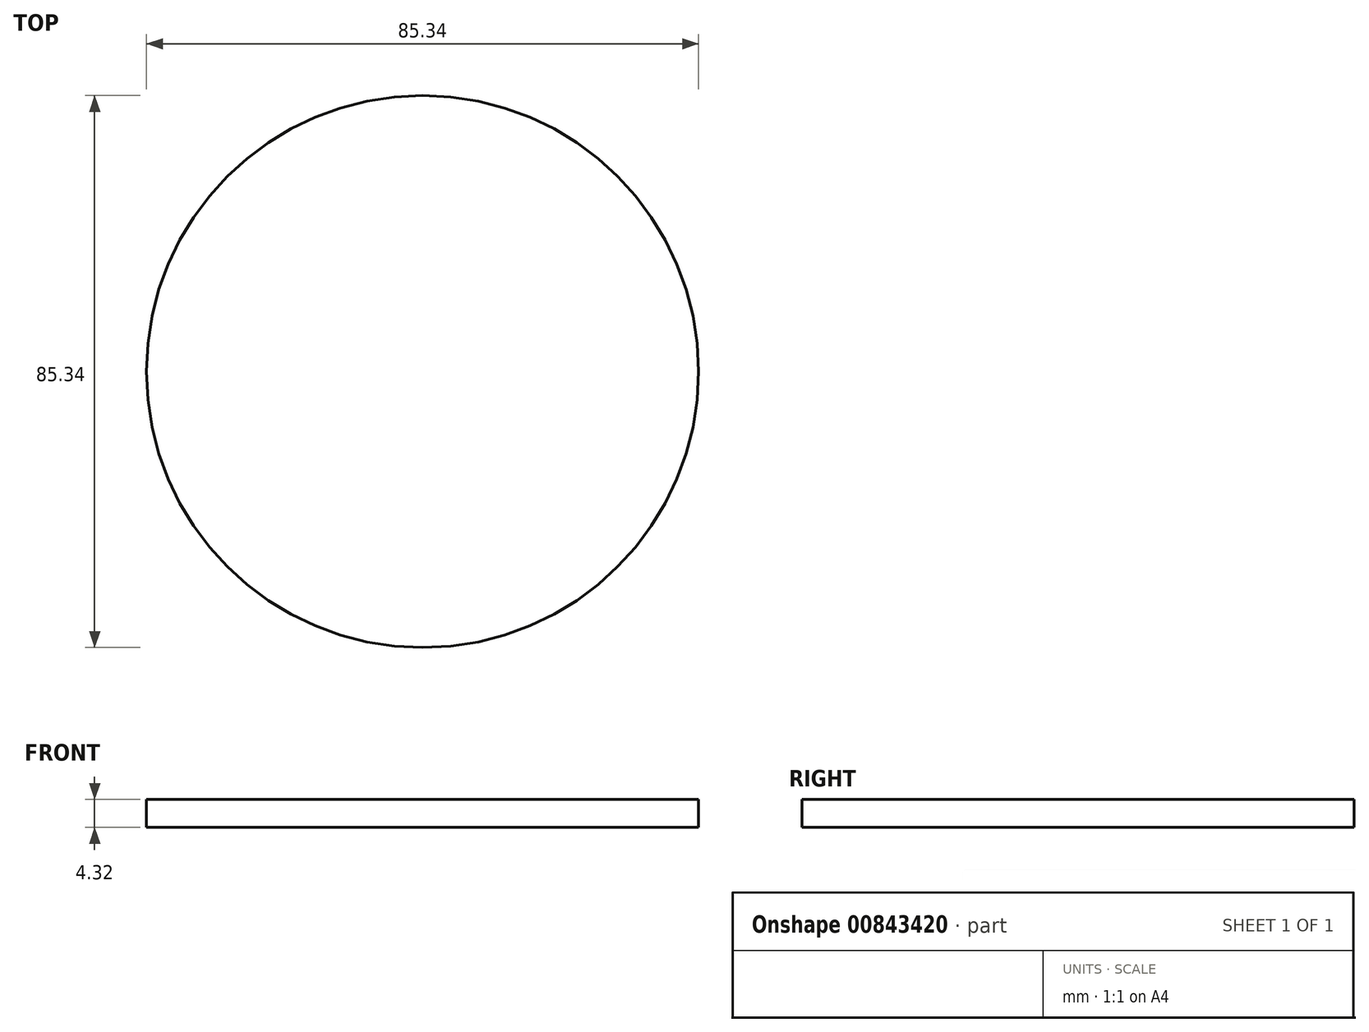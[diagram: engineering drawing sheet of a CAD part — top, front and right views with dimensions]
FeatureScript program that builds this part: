
annotation { "Feature Type Name" : "Feature", "Feature Type Description" : "" }
export const myFeature = defineFeature(function(context is Context, id is Id, definition is map)
    precondition{}
    {
        {
            var Q0;
            Q0=qCreatedBy(makeId("Top.planeOp"),FACE);
            var sketch = newSketch(context, id + "F0", { "sketchPlane" : qUnion([Q0])});
            skCircle(sketch, "E0", {"center": v(-45.73, 38.43) * mm, "radius": 42.67 * mm});
            skSolve(sketch);
        }
        {
            var Q0;
            Q0=makeQuery(id+"F0.imprint","IMPRINT",FACE,{"disambiguationData":[TD([[makeQuery(id+"F0.imprint","IMPRINT",EDGE,{"derivedFrom":sQuery(id+"F0.wireOp",EDGE,"E0")}),1.0]])]});
            extrude(context, id + "F1", {"entities" : qUnion([Q0]), "depth" : 4.32 * mm, "offsetDistance" : 25.4 * mm});
        }
    });
